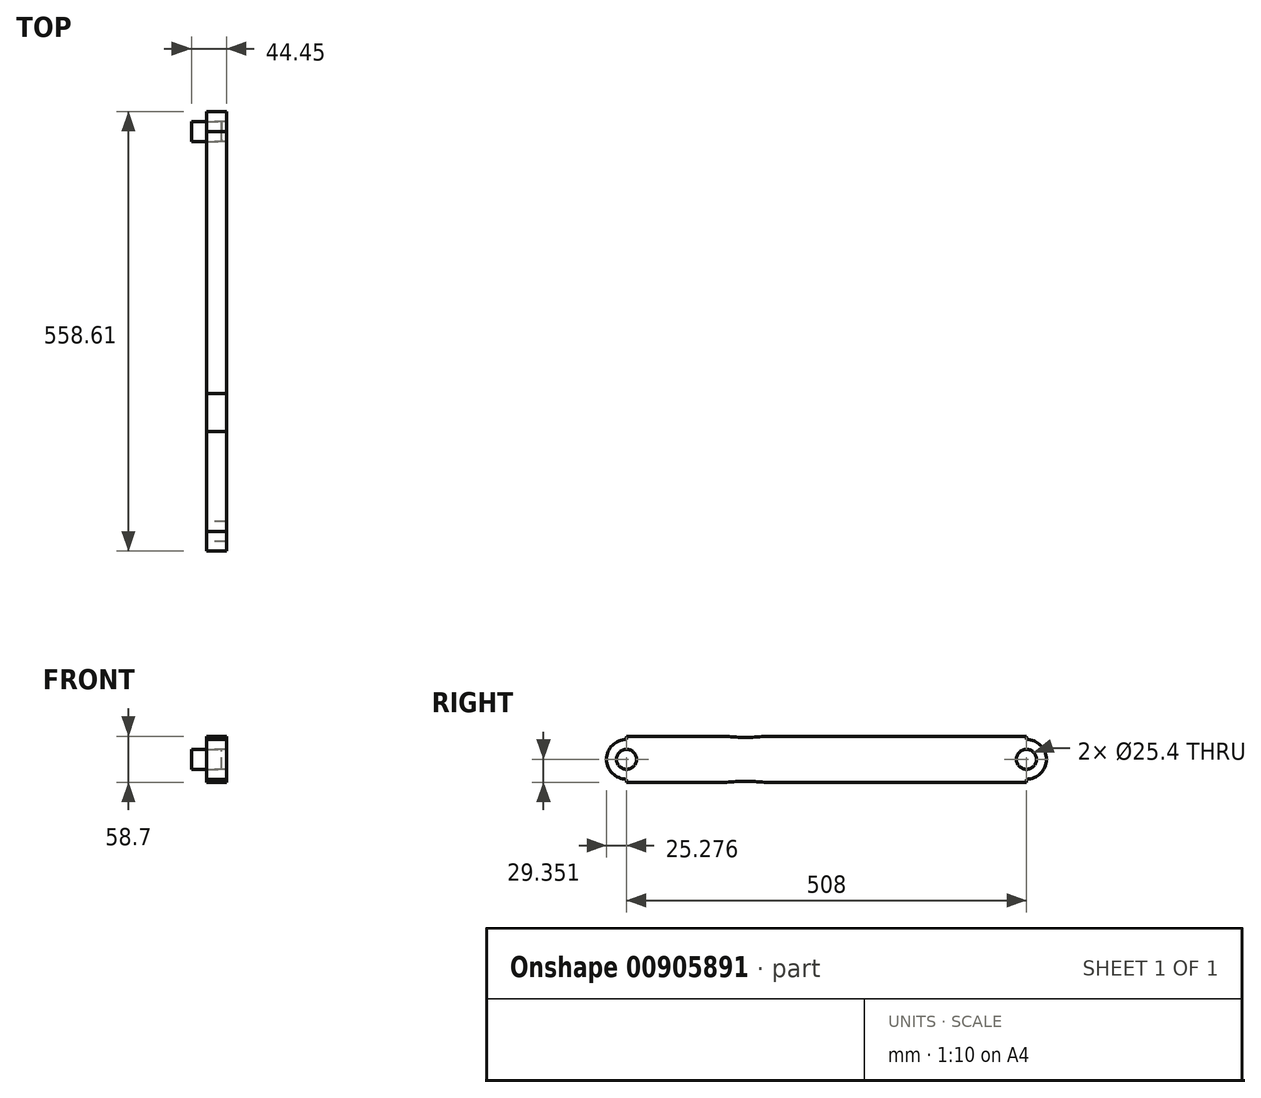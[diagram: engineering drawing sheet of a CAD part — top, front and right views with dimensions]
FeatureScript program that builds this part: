
annotation { "Feature Type Name" : "Feature", "Feature Type Description" : "" }
export const myFeature = defineFeature(function(context is Context, id is Id, definition is map)
    precondition{}
    {
        {
            var Q0;
            Q0=qCreatedBy(makeId("Right.planeOp"),FACE);
            var sketch = newSketch(context, id + "F0", { "sketchPlane" : qUnion([Q0])});
            skLineSegment(sketch, "E0.bottom", {"start": v(-36.86, 48.2) * mm, "end": v(90.14, 48.2) * mm});
            skLineSegment(sketch, "E0.top", {"start": v(-36.86, -10.51) * mm, "end": v(90.14, -10.51) * mm});
            skLineSegment(sketch, "E0.left", {"start": v(-36.86, 48.2) * mm, "end": v(-36.86, 31.54) * mm});
            skLineSegment(sketch, "E0.right", {"start": v(471.14, 48.2) * mm, "end": v(471.14, 31.54) * mm});
            skCircle(sketch, "E1", {"center": v(471.14, 18.84) * mm, "radius": 25.33 * mm});
            skCircle(sketch, "E2", {"center": v(-36.86, 18.84) * mm, "radius": 25.28 * mm});
            skCircle(sketch, "E3", {"center": v(471.14, 18.84) * mm, "radius": 12.7 * mm});
            skLineSegment(sketch, "E4.trimOffspring", {"start": v(471.14, 6.14) * mm, "end": v(471.14, -10.51) * mm});
            skCircle(sketch, "E5", {"center": v(-36.86, 18.84) * mm, "radius": 12.7 * mm});
            skLineSegment(sketch, "E6.trimOffspring", {"start": v(-36.86, 6.14) * mm, "end": v(-36.86, -10.51) * mm});
            skLineSegment(sketch, "E7", {"start": v(138.08, 48.2) * mm, "end": v(471.14, 48.2) * mm});
            skPoint(sketch, "E8", {"position": v(-194.98, 48.2) * mm});
            skPoint(sketch, "E9", {"position": v(138.08, 48.2) * mm});
            skPoint(sketch, "E10", {"position": v(90.14, 48.2) * mm});
            skArc(sketch, "E11", {"start": v(90.14, 48.2) * mm, "mid": v(114.1, 46.52) * mm, "end": v(138.08, 48.2) * mm});
            skPoint(sketch, "E12.orphan", {"position": v(217.14, 48.2) * mm});
            skPoint(sketch, "E13", {"position": v(138.08, -10.51) * mm});
            skPoint(sketch, "E14", {"position": v(90.14, -10.51) * mm});
            skLineSegment(sketch, "E15.trimOffspring", {"start": v(138.08, -10.51) * mm, "end": v(471.14, -10.51) * mm});
            skArc(sketch, "E16", {"start": v(138.08, -10.51) * mm, "mid": v(114.1, -9.23) * mm, "end": v(90.14, -10.51) * mm});
            skSolve(sketch);
        }
        {
            var Q0;
            Q0 = qSketchRegion(id + "F0", true);
            extrude(context, id + "F1", {"entities" : qUnion([Q0]), "depth" : 25.4 * mm, "offsetDistance" : 25.4 * mm});
        }
        {
            var Q0;
            Q0=makeQuery(id+"F1.opExtrude","CAP_FACE",FACE,{"disambiguationData":[OSD([sQuery(id+"F0.wireOp",EDGE,"E0.bottom"),sQuery(id+"F0.wireOp",EDGE,"E0.top"),sQuery(id+"F0.wireOp",EDGE,"E0.left"),sQuery(id+"F0.wireOp",EDGE,"E0.right"),sQuery(id+"F0.wireOp",EDGE,"E1"),sQuery(id+"F0.wireOp",EDGE,"E2"),sQuery(id+"F0.wireOp",EDGE,"E3"),sQuery(id+"F0.wireOp",EDGE,"E4.trimOffspring"),sQuery(id+"F0.wireOp",EDGE,"E5"),sQuery(id+"F0.wireOp",EDGE,"E6.trimOffspring"),sQuery(id+"F0.wireOp",EDGE,"E7"),sQuery(id+"F0.wireOp",EDGE,"E11"),sQuery(id+"F0.wireOp",EDGE,"E15.trimOffspring"),sQuery(id+"F0.wireOp",EDGE,"E16")])],"isStart":true});
            var sketch = newSketch(context, id + "F2", { "sketchPlane" : qUnion([Q0])});
            skCircle(sketch, "E17", {"center": v(-471.14, 18.84) * mm, "radius": 12.7 * mm});
            skSolve(sketch);
        }
        {
            var Q0;
            Q0=makeQuery(id+"F2.imprint","IMPRINT",FACE,{"disambiguationData":[TD([[makeQuery(id+"F2.imprint","IMPRINT",EDGE,{"derivedFrom":sQuery(id+"F2.wireOp",EDGE,"E17")}),-1.0]])]});
            extrude(context, id + "F3", {"entities" : qUnion([Q0]), "endBound" : BoundingType.SYMMETRIC, "depth" : 38.1 * mm, "offsetDistance" : 25.4 * mm});
        }
    });
